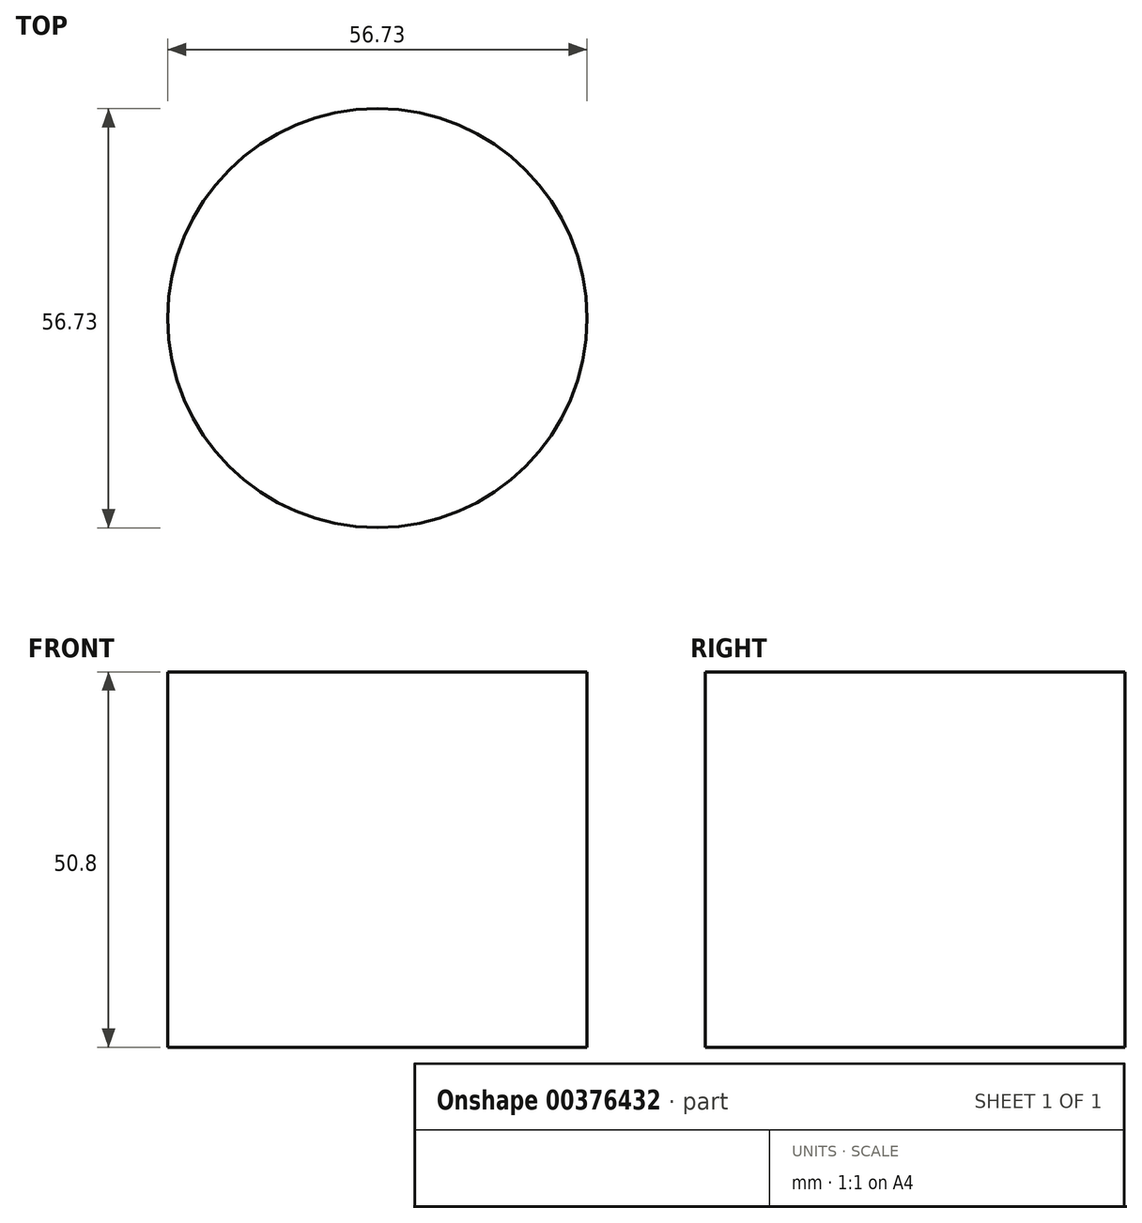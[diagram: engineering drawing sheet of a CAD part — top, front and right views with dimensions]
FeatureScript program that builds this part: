
annotation { "Feature Type Name" : "Feature", "Feature Type Description" : "" }
export const myFeature = defineFeature(function(context is Context, id is Id, definition is map)
    precondition{}
    {
        {
            var Q0;
            Q0=qCreatedBy(makeId("Top.planeOp"),FACE);
            var sketch = newSketch(context, id + "F0", { "sketchPlane" : qUnion([Q0])});
            skCircle(sketch, "E0", {"center": v(-37.74, -12.74) * mm, "radius": 28.37 * mm});
            skSolve(sketch);
        }
        {
            var Q0;
            Q0 = qSketchRegion(id + "F0", true);
            extrude(context, id + "F1", {"entities" : qUnion([Q0]), "depth" : 50.8 * mm});
        }
    });
